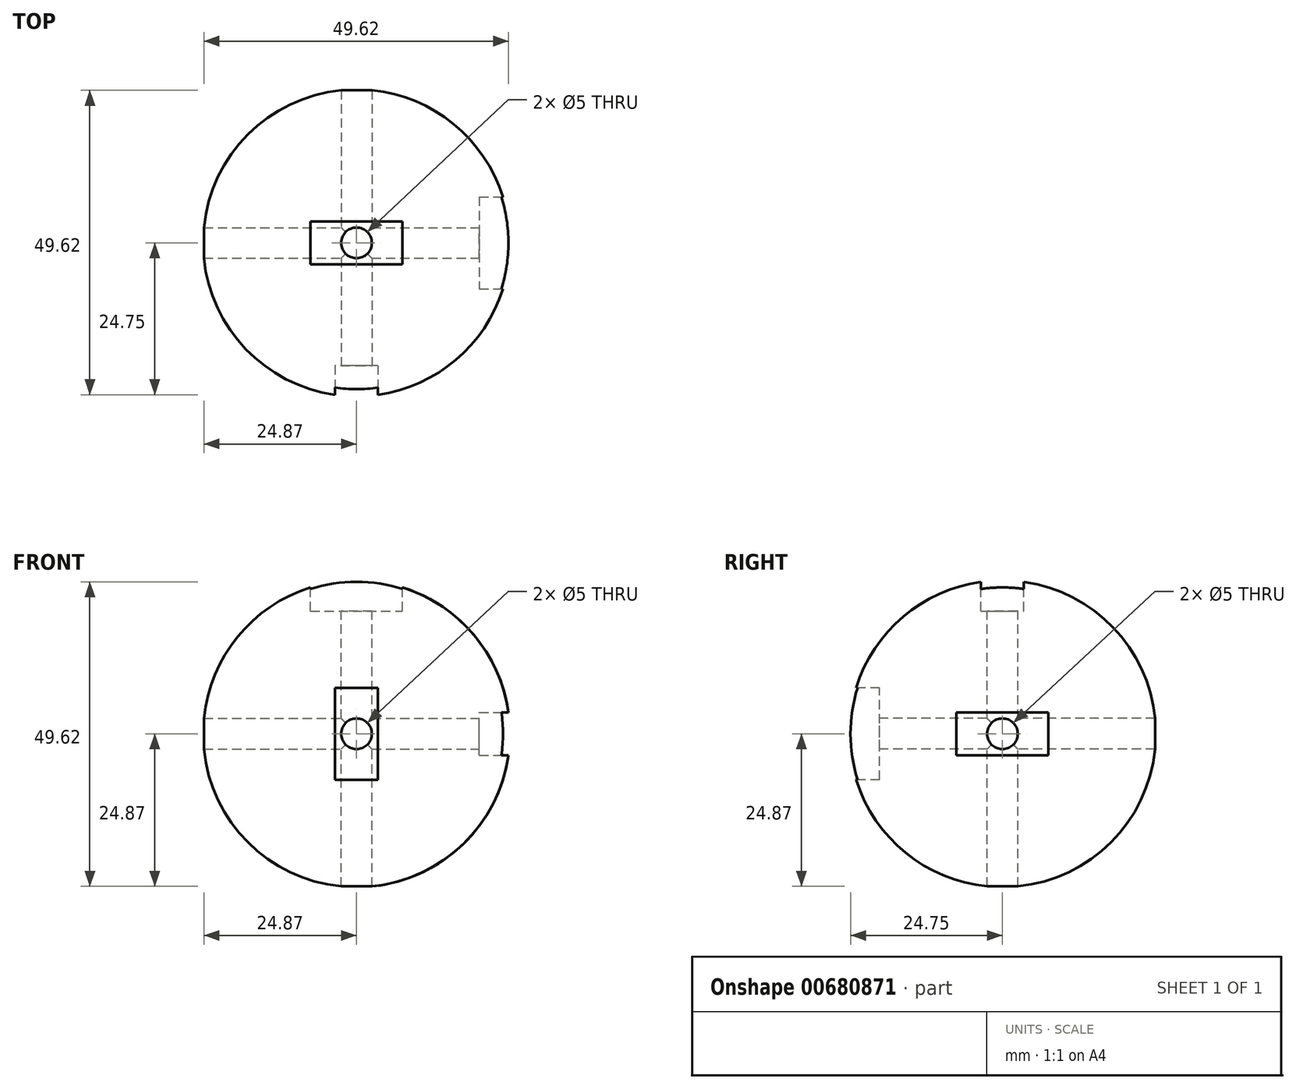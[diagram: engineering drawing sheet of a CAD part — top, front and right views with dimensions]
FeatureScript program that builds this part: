
annotation { "Feature Type Name" : "Feature", "Feature Type Description" : "" }
export const myFeature = defineFeature(function(context is Context, id is Id, definition is map)
    precondition{}
    {
        {
            var Q0;
            Q0=qCreatedBy(makeId("Front.planeOp"),FACE);
            var sketch = newSketch(context, id + "F0", { "sketchPlane" : qUnion([Q0])});
            skCircle(sketch, "E0", {"center": v(0, 0) * mm, "radius": 25 * mm});
            skLineSegment(sketch, "E1", {"start": v(0, 25) * mm, "end": v(0, -25) * mm});
            skSolve(sketch);
        }
        {
            var Q0;
            {var subQ0=sQuery(id+"F0.wireOp",EDGE,"E1");Q0=makeQuery(id+"F0.imprint","IMPRINT",FACE,{"disambiguationData":[TD([[makeQuery(id+"F0.imprint","IMPRINT",EDGE,{"derivedFrom":subQ0}),-1.0]])]});}
            var Q1;
            Q1=sQuery(id+"F0.wireOp",EDGE,"E1");
            revolve(context, id + "F1", {"entities" : qUnion([Q0]), "axis" : qUnion([Q1]), "revolveType" : RevolveType.FULL});
        }
        {
            var Q0;
            Q0=qCreatedBy(makeId("Front.planeOp"),FACE);
            cPlane(context, id + "F2", {"entities" : qUnion([Q0]), "cplaneType" : CPlaneType.OFFSET, "offset" : 25 * mm, "width" : 150 * mm, "height" : 150 * mm});
        }
        {
            var Q0;
            Q0=qCreatedBy(id+"F2.planeOp",FACE);
            var sketch = newSketch(context, id + "F3", { "sketchPlane" : qUnion([Q0])});
            skLineSegment(sketch, "E2.bottom", {"start": v(3.5, -7.5) * mm, "end": v(-3.5, -7.5) * mm});
            skLineSegment(sketch, "E2.top", {"start": v(3.5, 7.5) * mm, "end": v(-3.5, 7.5) * mm});
            skLineSegment(sketch, "E2.left", {"start": v(3.5, -7.5) * mm, "end": v(3.5, 7.5) * mm});
            skLineSegment(sketch, "E2.right", {"start": v(-3.5, -7.5) * mm, "end": v(-3.5, 7.5) * mm});
            skPoint(sketch, "E2.middle", {"position": v(0, 0) * mm});
            skSolve(sketch);
        }
        {
            var Q0;
            Q0 = qSketchRegion(id + "F3", true);
            extrude(context, id + "F4", {"entities" : qUnion([Q0]), "operationType" : NewBodyOperationType.REMOVE, "oppositeDirection" : true, "depth" : 5 * mm, "offsetDistance" : 25 * mm});
        }
        {
            var Q0;
            Q0=makeQuery(id+"F4.boolean.opBoolean","COPY",FACE,{"derivedFrom":makeQuery(id+"F4.opExtrude","CAP_FACE",FACE,{"disambiguationData":[OSD([sQuery(id+"F3.wireOp",EDGE,"E2.bottom"),sQuery(id+"F3.wireOp",EDGE,"E2.top"),sQuery(id+"F3.wireOp",EDGE,"E2.left"),sQuery(id+"F3.wireOp",EDGE,"E2.right")])],"isStart":false})});
            var sketch = newSketch(context, id + "F5", { "sketchPlane" : qUnion([Q0])});
            skCircle(sketch, "E3", {"center": v(0, 0) * mm, "radius": 2.5 * mm});
            skSolve(sketch);
        }
        {
            var Q0;
            Q0 = qSketchRegion(id + "F5", true);
            extrude(context, id + "F6", {"entities" : qUnion([Q0]), "operationType" : NewBodyOperationType.REMOVE, "endBound" : BoundingType.THROUGH_ALL, "oppositeDirection" : true, "depth" : 25 * mm, "offsetDistance" : 25 * mm});
        }
        {
            var Q0;
            Q0=qCreatedBy(makeId("Top.planeOp"),FACE);
            cPlane(context, id + "F7", {"entities" : qUnion([Q0]), "cplaneType" : CPlaneType.OFFSET, "offset" : 25 * mm, "width" : 150 * mm, "height" : 150 * mm});
        }
        {
            var Q0;
            Q0=qCreatedBy(id+"F7.planeOp",FACE);
            var sketch = newSketch(context, id + "F8", { "sketchPlane" : qUnion([Q0])});
            skLineSegment(sketch, "E4.bottom", {"start": v(-7.5, -3.5) * mm, "end": v(7.5, -3.5) * mm});
            skLineSegment(sketch, "E4.top", {"start": v(-7.5, 3.5) * mm, "end": v(7.5, 3.5) * mm});
            skLineSegment(sketch, "E4.left", {"start": v(-7.5, -3.5) * mm, "end": v(-7.5, 3.5) * mm});
            skLineSegment(sketch, "E4.right", {"start": v(7.5, -3.5) * mm, "end": v(7.5, 3.5) * mm});
            skPoint(sketch, "E4.middle", {"position": v(0, 0) * mm});
            skSolve(sketch);
        }
        {
            var Q0;
            Q0 = qSketchRegion(id + "F8", true);
            extrude(context, id + "F9", {"entities" : qUnion([Q0]), "operationType" : NewBodyOperationType.REMOVE, "oppositeDirection" : true, "depth" : 5 * mm, "offsetDistance" : 25 * mm});
        }
        {
            var Q0;
            Q0=makeQuery(id+"F9.boolean.opBoolean","COPY",FACE,{"derivedFrom":makeQuery(id+"F9.opExtrude","CAP_FACE",FACE,{"disambiguationData":[OSD([sQuery(id+"F8.wireOp",EDGE,"E4.bottom"),sQuery(id+"F8.wireOp",EDGE,"E4.top"),sQuery(id+"F8.wireOp",EDGE,"E4.left"),sQuery(id+"F8.wireOp",EDGE,"E4.right")])],"isStart":false})});
            var sketch = newSketch(context, id + "F10", { "sketchPlane" : qUnion([Q0])});
            skCircle(sketch, "E5", {"center": v(0, 0) * mm, "radius": 2.5 * mm});
            skSolve(sketch);
        }
        {
            var Q0;
            Q0 = qSketchRegion(id + "F10", true);
            extrude(context, id + "F11", {"entities" : qUnion([Q0]), "operationType" : NewBodyOperationType.REMOVE, "endBound" : BoundingType.THROUGH_ALL, "oppositeDirection" : true, "depth" : 25 * mm, "offsetDistance" : 25 * mm});
        }
        {
            var Q0;
            Q0=qCreatedBy(makeId("Right.planeOp"),FACE);
            cPlane(context, id + "F12", {"entities" : qUnion([Q0]), "cplaneType" : CPlaneType.OFFSET, "offset" : 25 * mm, "width" : 150 * mm, "height" : 150 * mm});
        }
        {
            var Q0;
            Q0=qCreatedBy(id+"F12.planeOp",FACE);
            var sketch = newSketch(context, id + "F13", { "sketchPlane" : qUnion([Q0])});
            skLineSegment(sketch, "E6.bottom", {"start": v(7.5, -3.5) * mm, "end": v(-7.5, -3.5) * mm});
            skLineSegment(sketch, "E6.top", {"start": v(7.5, 3.5) * mm, "end": v(-7.5, 3.5) * mm});
            skLineSegment(sketch, "E6.left", {"start": v(7.5, -3.5) * mm, "end": v(7.5, 3.5) * mm});
            skLineSegment(sketch, "E6.right", {"start": v(-7.5, -3.5) * mm, "end": v(-7.5, 3.5) * mm});
            skPoint(sketch, "E6.middle", {"position": v(0, 0) * mm});
            skSolve(sketch);
        }
        {
            var Q0;
            Q0 = qSketchRegion(id + "F13", true);
            extrude(context, id + "F14", {"entities" : qUnion([Q0]), "operationType" : NewBodyOperationType.REMOVE, "oppositeDirection" : true, "depth" : 5 * mm, "offsetDistance" : 25 * mm});
        }
        {
            var Q0;
            Q0=makeQuery(id+"F14.boolean.opBoolean","COPY",FACE,{"derivedFrom":makeQuery(id+"F14.opExtrude","CAP_FACE",FACE,{"disambiguationData":[OSD([sQuery(id+"F13.wireOp",EDGE,"E6.bottom"),sQuery(id+"F13.wireOp",EDGE,"E6.top"),sQuery(id+"F13.wireOp",EDGE,"E6.left"),sQuery(id+"F13.wireOp",EDGE,"E6.right")])],"isStart":false})});
            var sketch = newSketch(context, id + "F15", { "sketchPlane" : qUnion([Q0])});
            skCircle(sketch, "E7", {"center": v(0, 0) * mm, "radius": 2.5 * mm});
            skSolve(sketch);
        }
        {
            var Q0;
            Q0 = qSketchRegion(id + "F15", true);
            extrude(context, id + "F16", {"entities" : qUnion([Q0]), "operationType" : NewBodyOperationType.REMOVE, "endBound" : BoundingType.THROUGH_ALL, "oppositeDirection" : true, "depth" : 25 * mm, "offsetDistance" : 25 * mm});
        }
    });
